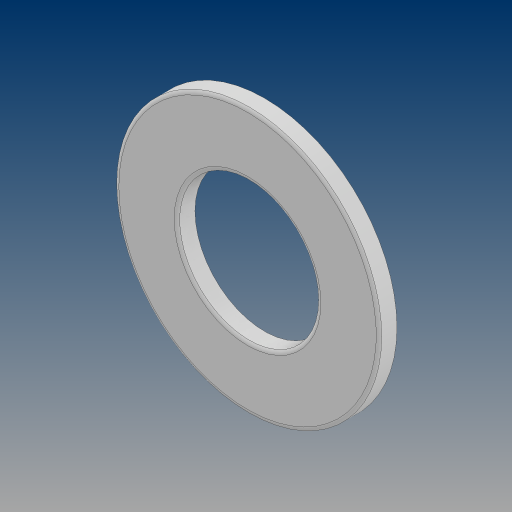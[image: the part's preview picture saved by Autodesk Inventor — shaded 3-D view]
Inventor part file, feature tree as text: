
AUTODESK INVENTOR PART (.ipt)
format: ipt  version: 2024.3 (Build 283343000, 343)  size: 120,320 bytes
history: native  units: in
note: dims shown in document units (in); Inventor stores cm internally (conversion verified against a paired STEP export)
features: fillet x1
ambient origin geometry x8: Origin, YZ Plane, XZ Plane, XY Plane, X Axis, Y Axis, Z Axis, Center Point
bodies: Solid1 (feature_tree)
feature tree (1):
  fillet  "Fillet1"  [1 undecoded]
note: 1 required parameter value undecoded (feature->parameter linkage not recoverable at this tier; creation-order binding heuristic only, values carry confidence <= 0.55)
